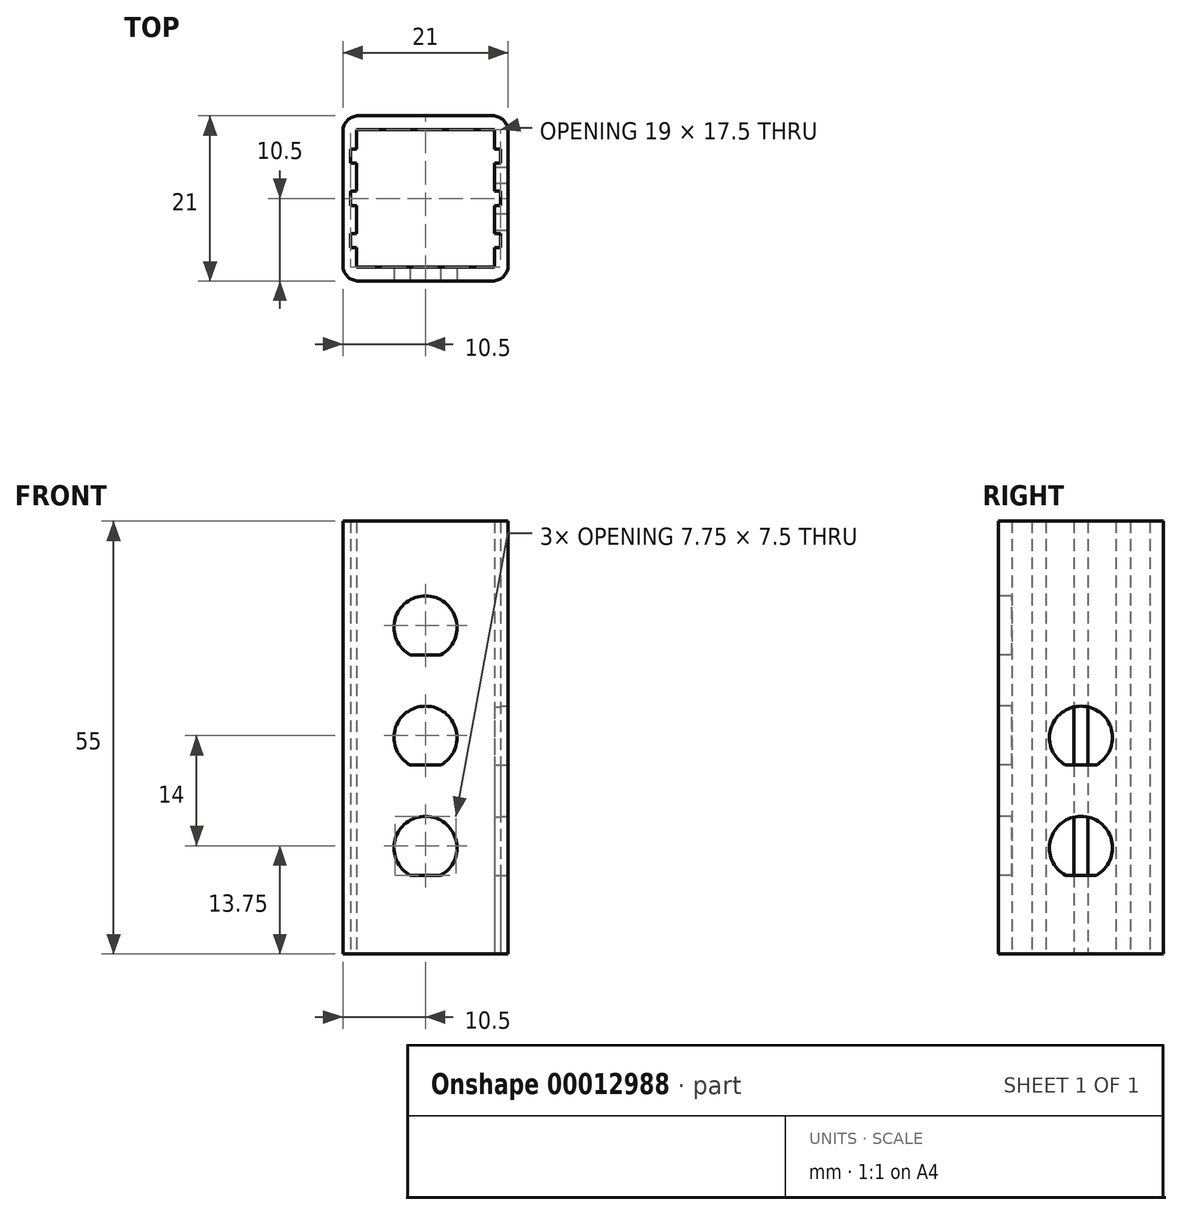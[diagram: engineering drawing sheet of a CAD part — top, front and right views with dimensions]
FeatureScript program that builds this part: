
annotation { "Feature Type Name" : "Feature", "Feature Type Description" : "" }
export const myFeature = defineFeature(function(context is Context, id is Id, definition is map)
    precondition{}
    {
        {
            var Q0;
            Q0=qCreatedBy(makeId("Top.planeOp"),FACE);
            var sketch = newSketch(context, id + "F0", { "sketchPlane" : qUnion([Q0])});
            skLineSegment(sketch, "E0.rect.bottom", {"start": v(10.5, 10.5) * mm, "end": v(-10.5, 10.5) * mm});
            skLineSegment(sketch, "E0.rect.top", {"start": v(10.5, -10.5) * mm, "end": v(-10.5, -10.5) * mm});
            skLineSegment(sketch, "E0.rect.left", {"start": v(10.5, 10.5) * mm, "end": v(10.5, -10.5) * mm});
            skLineSegment(sketch, "E0.rect.right", {"start": v(-10.5, 10.5) * mm, "end": v(-10.5, -10.5) * mm});
            skPoint(sketch, "E0.rect.middle", {"position": v(0, 0) * mm});
            skLineSegment(sketch, "E1.rect.bottom", {"start": v(8.75, -8.75) * mm, "end": v(-8.75, -8.75) * mm});
            skLineSegment(sketch, "E1.rect.top", {"start": v(8.75, 8.75) * mm, "end": v(-8.75, 8.75) * mm});
            skLineSegment(sketch, "E1.rect.left", {"start": v(8.75, -8.75) * mm, "end": v(8.75, 8.75) * mm});
            skLineSegment(sketch, "E1.rect.right", {"start": v(-8.75, -8.75) * mm, "end": v(-8.75, 8.75) * mm});
            skLineSegment(sketch, "E2.bottom", {"start": v(-8.75, 6.25) * mm, "end": v(-9.5, 6.25) * mm});
            skLineSegment(sketch, "E2.top", {"start": v(-8.75, 4.45) * mm, "end": v(-9.5, 4.45) * mm});
            skLineSegment(sketch, "E2.left", {"start": v(-8.75, 6.25) * mm, "end": v(-8.75, 4.45) * mm});
            skLineSegment(sketch, "E2.right", {"start": v(-9.5, 6.25) * mm, "end": v(-9.5, 4.45) * mm});
            skLineSegment(sketch, "E3.bottom", {"start": v(8.75, 6.25) * mm, "end": v(9.5, 6.25) * mm});
            skLineSegment(sketch, "E3.top", {"start": v(8.75, 4.45) * mm, "end": v(9.5, 4.45) * mm});
            skLineSegment(sketch, "E3.left", {"start": v(8.75, 6.25) * mm, "end": v(8.75, 4.45) * mm});
            skLineSegment(sketch, "E3.right", {"start": v(9.5, 6.25) * mm, "end": v(9.5, 4.45) * mm});
            skLineSegment(sketch, "E4", {"start": v(-9.5, 6.25) * mm, "end": v(-9.5, 10.5) * mm, "construction": true});
            skLineSegment(sketch, "E5", {"start": v(-10.5, 0) * mm, "end": v(10.5, 0) * mm});
            skLineSegment(sketch, "E6.rect.bottom", {"start": v(-8.75, -0.9) * mm, "end": v(-9.5, -0.9) * mm});
            skLineSegment(sketch, "E6.rect.top", {"start": v(-8.75, 0.9) * mm, "end": v(-9.5, 0.9) * mm});
            skLineSegment(sketch, "E6.rect.left", {"start": v(-8.75, -0.9) * mm, "end": v(-8.75, 0.9) * mm});
            skLineSegment(sketch, "E6.rect.right", {"start": v(-9.5, -0.9) * mm, "end": v(-9.5, 0.9) * mm});
            skPoint(sketch, "E6.rect.middle", {"position": v(-9.13, 0) * mm});
            skLineSegment(sketch, "E7.rect.bottom", {"start": v(8.75, -0.9) * mm, "end": v(9.5, -0.9) * mm});
            skLineSegment(sketch, "E7.rect.top", {"start": v(8.75, 0.9) * mm, "end": v(9.5, 0.9) * mm});
            skLineSegment(sketch, "E7.rect.left", {"start": v(8.75, -0.9) * mm, "end": v(8.75, 0.9) * mm});
            skLineSegment(sketch, "E7.rect.right", {"start": v(9.5, -0.9) * mm, "end": v(9.5, 0.9) * mm});
            skPoint(sketch, "E7.rect.middle", {"position": v(9.13, 0) * mm});
            skLineSegment(sketch, "E8.bottom", {"start": v(-8.75, -4.45) * mm, "end": v(-9.5, -4.45) * mm});
            skLineSegment(sketch, "E8.top", {"start": v(-8.75, -6.25) * mm, "end": v(-9.5, -6.25) * mm});
            skLineSegment(sketch, "E8.left", {"start": v(-8.75, -4.45) * mm, "end": v(-8.75, -6.25) * mm});
            skLineSegment(sketch, "E8.right", {"start": v(-9.5, -4.45) * mm, "end": v(-9.5, -6.25) * mm});
            skLineSegment(sketch, "E9.bottom", {"start": v(8.75, -4.45) * mm, "end": v(9.5, -4.45) * mm});
            skLineSegment(sketch, "E9.top", {"start": v(8.75, -6.25) * mm, "end": v(9.5, -6.25) * mm});
            skLineSegment(sketch, "E9.left", {"start": v(8.75, -4.45) * mm, "end": v(8.75, -6.25) * mm});
            skLineSegment(sketch, "E9.right", {"start": v(9.5, -4.45) * mm, "end": v(9.5, -6.25) * mm});
            skLineSegment(sketch, "E10", {"start": v(-9.5, -6.25) * mm, "end": v(-9.5, -10.5) * mm, "construction": true});
            skSolve(sketch);
        }
        {
            var Q0;
            Q0=makeQuery(id+"F0.imprint","IMPRINT",FACE,{"disambiguationData":[TD([[makeQuery(id+"F0.imprint","IMPRINT",EDGE,{"derivedFrom":sQuery(id+"F0.wireOp",EDGE,"E0.rect.bottom")}),1.0]])]});
            var Q1;
            {var subQ14=sQuery(id+"F0.wireOp",EDGE,"E0.rect.top");Q1=makeQuery(id+"F0.imprint","IMPRINT",FACE,{"disambiguationData":[TD([[makeQuery(id+"F0.imprint","IMPRINT",EDGE,{"derivedFrom":subQ14}),-1.0]])]});}
            extrude(context, id + "F1", {"entities" : qUnion([Q0, Q1]), "depth" : 55 * mm});
        }
        {
            var Q0;
            Q0=makeQuery(id+"F1.opExtrude","SWEPT_FACE",FACE,{"disambiguationData":[OSD([sQuery(id+"F0.wireOp",EDGE,"E0.rect.top")])]});
            var sketch = newSketch(context, id + "F2", { "sketchPlane" : qUnion([Q0])});
            skLineSegment(sketch, "E11", {"start": v(-10.5, 27.5) * mm, "end": v(10.5, 27.5) * mm, "construction": true});
            skCircle(sketch, "E12", {"center": v(0, 27.5) * mm, "radius": 4 * mm});
            skCircle(sketch, "E13", {"center": v(0, 41.5) * mm, "radius": 4 * mm});
            skCircle(sketch, "E14.0.MirrorC", {"center": v(0, 13.5) * mm, "radius": 4 * mm});
            skLineSegment(sketch, "E15.bottom", {"start": v(-1.94, 38) * mm, "end": v(1.94, 38) * mm});
            skLineSegment(sketch, "E15.top", {"start": v(-1.94, 37.5) * mm, "end": v(1.94, 37.5) * mm});
            skLineSegment(sketch, "E15.left", {"start": v(-1.94, 38) * mm, "end": v(-1.94, 37.5) * mm});
            skLineSegment(sketch, "E15.right", {"start": v(1.94, 38) * mm, "end": v(1.94, 37.5) * mm});
            skLineSegment(sketch, "E16", {"start": v(0, 41.5) * mm, "end": v(0, 37.5) * mm, "construction": true});
            skLineSegment(sketch, "E17", {"start": v(0, 27.5) * mm, "end": v(0, 23.5) * mm, "construction": true});
            skLineSegment(sketch, "E18", {"start": v(0, 13.5) * mm, "end": v(0, 9.5) * mm, "construction": true});
            skLineSegment(sketch, "E19.bottom", {"start": v(-1.94, 24) * mm, "end": v(1.94, 24) * mm});
            skLineSegment(sketch, "E19.top", {"start": v(-1.94, 23.5) * mm, "end": v(1.94, 23.5) * mm});
            skLineSegment(sketch, "E19.left", {"start": v(-1.94, 24) * mm, "end": v(-1.94, 23.5) * mm});
            skLineSegment(sketch, "E19.right", {"start": v(1.94, 24) * mm, "end": v(1.94, 23.5) * mm});
            skLineSegment(sketch, "E20.bottom", {"start": v(-1.94, 10) * mm, "end": v(1.94, 10) * mm});
            skLineSegment(sketch, "E20.top", {"start": v(-1.94, 9.5) * mm, "end": v(1.94, 9.5) * mm});
            skLineSegment(sketch, "E20.left", {"start": v(-1.94, 10) * mm, "end": v(-1.94, 9.5) * mm});
            skLineSegment(sketch, "E20.right", {"start": v(1.94, 10) * mm, "end": v(1.94, 9.5) * mm});
            skSolve(sketch);
        }
        {
            var Q0;
            Q0=makeQuery(id+"F1.opExtrude","SWEPT_FACE",FACE,{"disambiguationData":[OSD([sQuery(id+"F0.wireOp",EDGE,"E0.rect.left")])]});
            var sketch = newSketch(context, id + "F3", { "sketchPlane" : qUnion([Q0])});
            skLineSegment(sketch, "E21", {"start": v(-10.5, 27.5) * mm, "end": v(10.5, 27.5) * mm, "construction": true});
            skCircle(sketch, "E22", {"center": v(0, 27.5) * mm, "radius": 4 * mm});
            skCircle(sketch, "E23", {"center": v(0, 13.5) * mm, "radius": 4 * mm});
            skLineSegment(sketch, "E24", {"start": v(0, 27.5) * mm, "end": v(0, 23.5) * mm, "construction": true});
            skLineSegment(sketch, "E25", {"start": v(0, 13.5) * mm, "end": v(0, 9.5) * mm, "construction": true});
            skLineSegment(sketch, "E26.bottom", {"start": v(-1.94, 24) * mm, "end": v(1.94, 24) * mm});
            skLineSegment(sketch, "E26.top", {"start": v(-1.94, 23.5) * mm, "end": v(1.94, 23.5) * mm});
            skLineSegment(sketch, "E26.left", {"start": v(-1.94, 24) * mm, "end": v(-1.94, 23.5) * mm});
            skLineSegment(sketch, "E26.right", {"start": v(1.94, 24) * mm, "end": v(1.94, 23.5) * mm});
            skLineSegment(sketch, "E27.bottom", {"start": v(-1.94, 10) * mm, "end": v(1.94, 10) * mm});
            skLineSegment(sketch, "E27.top", {"start": v(-1.94, 9.5) * mm, "end": v(1.94, 9.5) * mm});
            skLineSegment(sketch, "E27.left", {"start": v(-1.94, 10) * mm, "end": v(-1.94, 9.5) * mm});
            skLineSegment(sketch, "E27.right", {"start": v(1.94, 10) * mm, "end": v(1.94, 9.5) * mm});
            skSolve(sketch);
        }
        {
            var Q0;
            {var subQ3=sQuery(id+"F2.wireOp",EDGE,"E19.bottom");Q0=makeQuery(id+"F2.imprint","IMPRINT",FACE,{"disambiguationData":[TD([[makeQuery(id+"F2.imprint","IMPRINT",EDGE,{"derivedFrom":subQ3}),1.0]])]});}
            var Q1;
            {var subQ3=sQuery(id+"F2.wireOp",EDGE,"E15.bottom");Q1=makeQuery(id+"F2.imprint","IMPRINT",FACE,{"disambiguationData":[TD([[makeQuery(id+"F2.imprint","IMPRINT",EDGE,{"derivedFrom":subQ3}),1.0]])]});}
            var Q2;
            {var subQ3=sQuery(id+"F2.wireOp",EDGE,"E20.bottom");Q2=makeQuery(id+"F2.imprint","IMPRINT",FACE,{"disambiguationData":[TD([[makeQuery(id+"F2.imprint","IMPRINT",EDGE,{"derivedFrom":subQ3}),1.0]])]});}
            extrude(context, id + "F4", {"entities" : qUnion([Q0, Q1, Q2]), "operationType" : NewBodyOperationType.REMOVE, "endBound" : BoundingType.UP_TO_NEXT, "oppositeDirection" : true, "depth" : 25 * mm});
        }
        {
            var Q0;
            {var subQ3=sQuery(id+"F3.wireOp",EDGE,"E26.bottom");Q0=makeQuery(id+"F3.imprint","IMPRINT",FACE,{"disambiguationData":[TD([[makeQuery(id+"F3.imprint","IMPRINT",EDGE,{"derivedFrom":subQ3}),1.0]])]});}
            var Q1;
            {var subQ3=sQuery(id+"F3.wireOp",EDGE,"E27.bottom");Q1=makeQuery(id+"F3.imprint","IMPRINT",FACE,{"disambiguationData":[TD([[makeQuery(id+"F3.imprint","IMPRINT",EDGE,{"derivedFrom":subQ3}),1.0]])]});}
            extrude(context, id + "F5", {"entities" : qUnion([Q0, Q1]), "operationType" : NewBodyOperationType.REMOVE, "endBound" : BoundingType.UP_TO_NEXT, "oppositeDirection" : true, "depth" : 25 * mm});
        }
        {
            var Q0;
            Q0=makeQuery(id+"F1.opExtrude","SWEPT_EDGE",EDGE,{"disambiguationData":[OSD([sQuery(id+"F0.wireOp",EDGE,"E0.rect.top"),sQuery(id+"F0.wireOp",EDGE,"E0.rect.right")])]});
            var Q1;
            Q1=makeQuery(id+"F1.opExtrude","SWEPT_EDGE",EDGE,{"disambiguationData":[OSD([sQuery(id+"F0.wireOp",EDGE,"E0.rect.top"),sQuery(id+"F0.wireOp",EDGE,"E0.rect.left")])]});
            var Q2;
            Q2=makeQuery(id+"F1.opExtrude","SWEPT_EDGE",EDGE,{"disambiguationData":[OSD([sQuery(id+"F0.wireOp",EDGE,"E0.rect.bottom"),sQuery(id+"F0.wireOp",EDGE,"E0.rect.left")])]});
            var Q3;
            Q3=makeQuery(id+"F1.opExtrude","SWEPT_EDGE",EDGE,{"disambiguationData":[OSD([sQuery(id+"F0.wireOp",EDGE,"E0.rect.bottom"),sQuery(id+"F0.wireOp",EDGE,"E0.rect.right")])]});
            fillet(context, id + "F6", {"entities" : qUnion([Q0, Q1, Q2, Q3]), "radius" : 2 * mm, "tangentPropagation" : true, "allowEdgeOverflow" : false});
        }
    });
